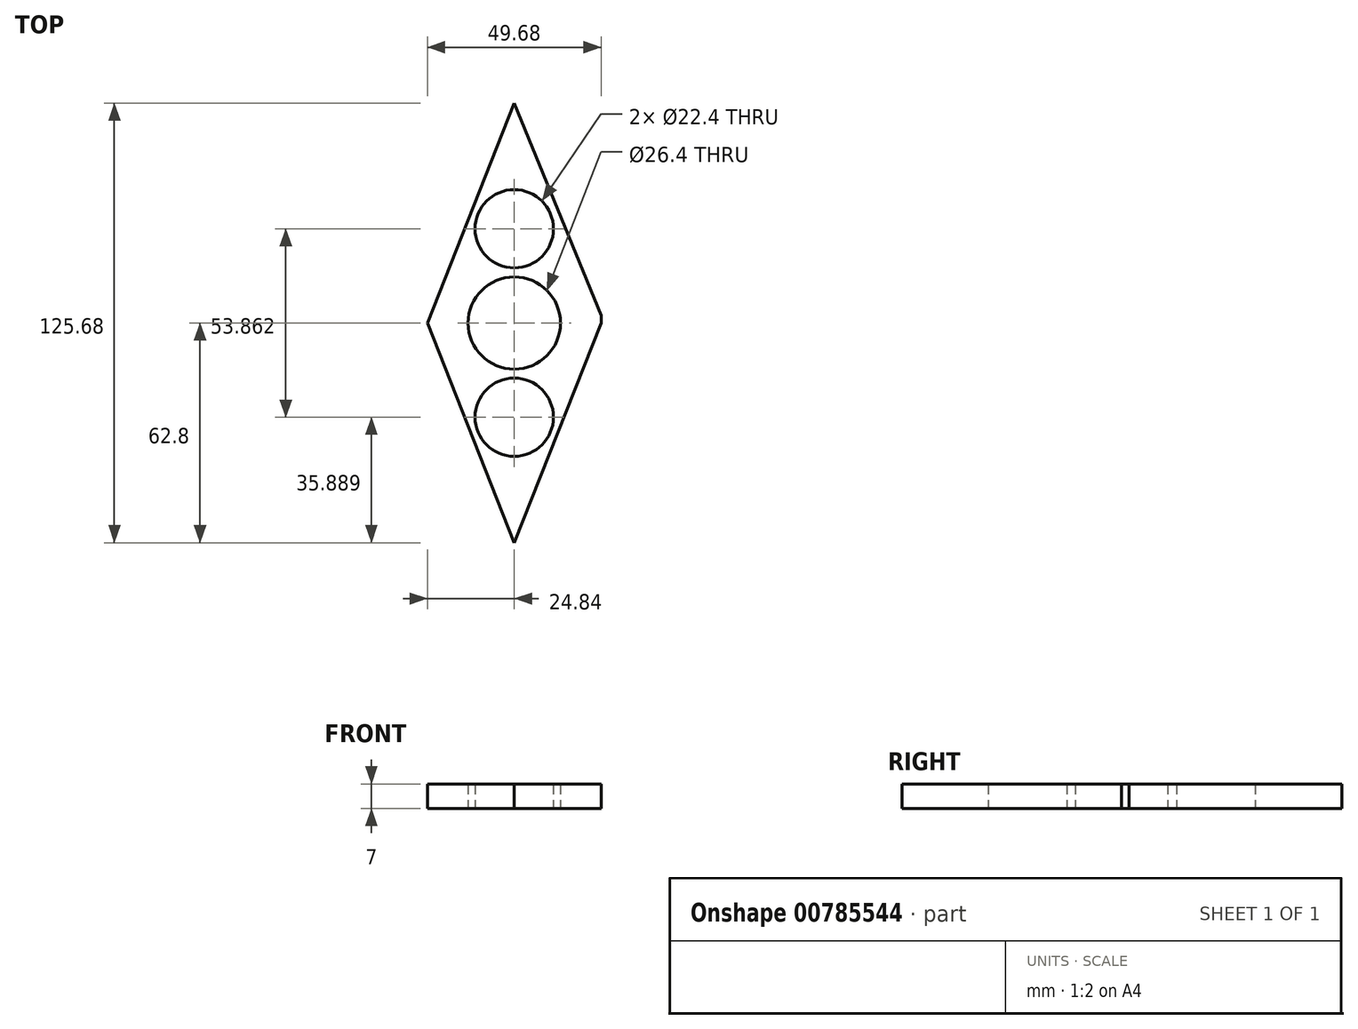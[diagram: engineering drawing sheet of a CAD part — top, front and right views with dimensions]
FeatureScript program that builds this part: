
annotation { "Feature Type Name" : "Feature", "Feature Type Description" : "" }
export const myFeature = defineFeature(function(context is Context, id is Id, definition is map)
    precondition{}
    {
        {
            var Q0;
            Q0=qCreatedBy(makeId("Top.planeOp"),FACE);
            var sketch = newSketch(context, id + "F0", { "sketchPlane" : qUnion([Q0])});
            skCircle(sketch, "E0", {"center": v(0, 0) * mm, "radius": 11.2 * mm});
            skCircle(sketch, "E1", {"center": v(0, 26.95) * mm, "radius": 11.2 * mm});
            skCircle(sketch, "E2", {"center": v(0, -26.91) * mm, "radius": 11.2 * mm});
            skCircle(sketch, "E3", {"center": v(0, 26.95) * mm, "radius": 13.2 * mm});
            skCircle(sketch, "E4", {"center": v(0, 0) * mm, "radius": 13.2 * mm});
            skCircle(sketch, "E5", {"center": v(0, -26.91) * mm, "radius": 13.2 * mm});
            skLineSegment(sketch, "E6", {"start": v(0, 62.88) * mm, "end": v(-24.84, 0) * mm});
            skLineSegment(sketch, "E7", {"start": v(-24.84, 0) * mm, "end": v(0, -62.8) * mm});
            skLineSegment(sketch, "E8", {"start": v(0, -62.8) * mm, "end": v(24.84, 0) * mm});
            skLineSegment(sketch, "E9", {"start": v(0, 62.88) * mm, "end": v(24.84, 2.13) * mm});
            skLineSegment(sketch, "E10", {"start": v(24.84, 2.13) * mm, "end": v(24.84, 0) * mm});
            skSolve(sketch);
        }
        {
            var Q0;
            Q0 = qSketchRegion(id + "F0", true);
            extrude(context, id + "F1", {"entities" : qUnion([Q0]), "depth" : 7 * mm, "offsetDistance" : 25 * mm});
        }
    });
